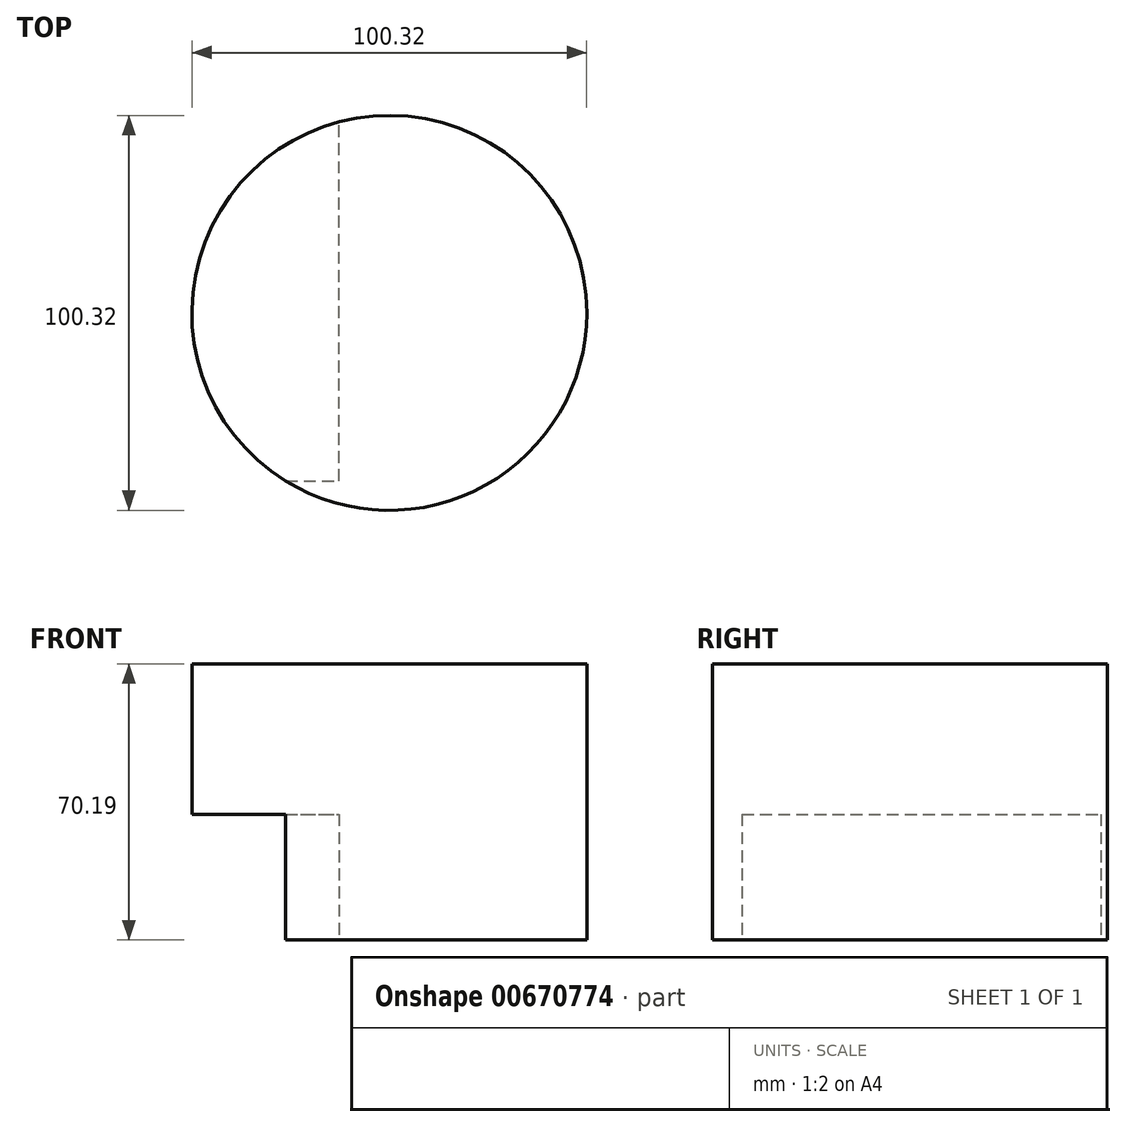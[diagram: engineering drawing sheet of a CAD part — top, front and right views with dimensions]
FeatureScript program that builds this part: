
annotation { "Feature Type Name" : "Feature", "Feature Type Description" : "" }
export const myFeature = defineFeature(function(context is Context, id is Id, definition is map)
    precondition{}
    {
        {
            var Q0;
            Q0=qCreatedBy(makeId("Top.planeOp"),FACE);
            var sketch = newSketch(context, id + "F0", { "sketchPlane" : qUnion([Q0])});
            skCircle(sketch, "E0", {"center": v(0, 0) * mm, "radius": 50.16 * mm});
            skSolve(sketch);
        }
        {
            var Q0;
            Q0 = qSketchRegion(id + "F0", true);
            extrude(context, id + "F1", {"entities" : qUnion([Q0]), "depth" : 70.19 * mm, "offsetDistance" : 25.4 * mm});
        }
        {
            var Q0;
            Q0=makeQuery(id+"F1.opExtrude","CAP_FACE",FACE,{"disambiguationData":[OSD([sQuery(id+"F0.wireOp",EDGE,"E0")])],"isStart":false});
            var sketch = newSketch(context, id + "F2", { "sketchPlane" : qUnion([Q0])});
            skSolve(sketch);
        }
        {
            var Q0;
            Q0=makeQuery(id+"F1.opExtrude","CAP_FACE",FACE,{"disambiguationData":[OSD([sQuery(id+"F0.wireOp",EDGE,"E0")])],"isStart":true});
            var sketch = newSketch(context, id + "F3", { "sketchPlane" : qUnion([Q0])});
            skLineSegment(sketch, "E1.bottom", {"start": v(-89.45, 42.72) * mm, "end": v(-12.78, 42.72) * mm});
            skLineSegment(sketch, "E1.top", {"start": v(-89.45, -48.5) * mm, "end": v(-12.78, -48.5) * mm});
            skLineSegment(sketch, "E1.left", {"start": v(-89.45, 42.72) * mm, "end": v(-89.45, -48.5) * mm});
            skLineSegment(sketch, "E1.right", {"start": v(-12.78, 42.72) * mm, "end": v(-12.78, -48.5) * mm});
            skSolve(sketch);
        }
        {
            var Q0;
            Q0 = qSketchRegion(id + "F3", true);
            extrude(context, id + "F4", {"entities" : qUnion([Q0]), "operationType" : NewBodyOperationType.REMOVE, "oppositeDirection" : true, "depth" : 31.97 * mm, "offsetDistance" : 25.4 * mm});
        }
    });
